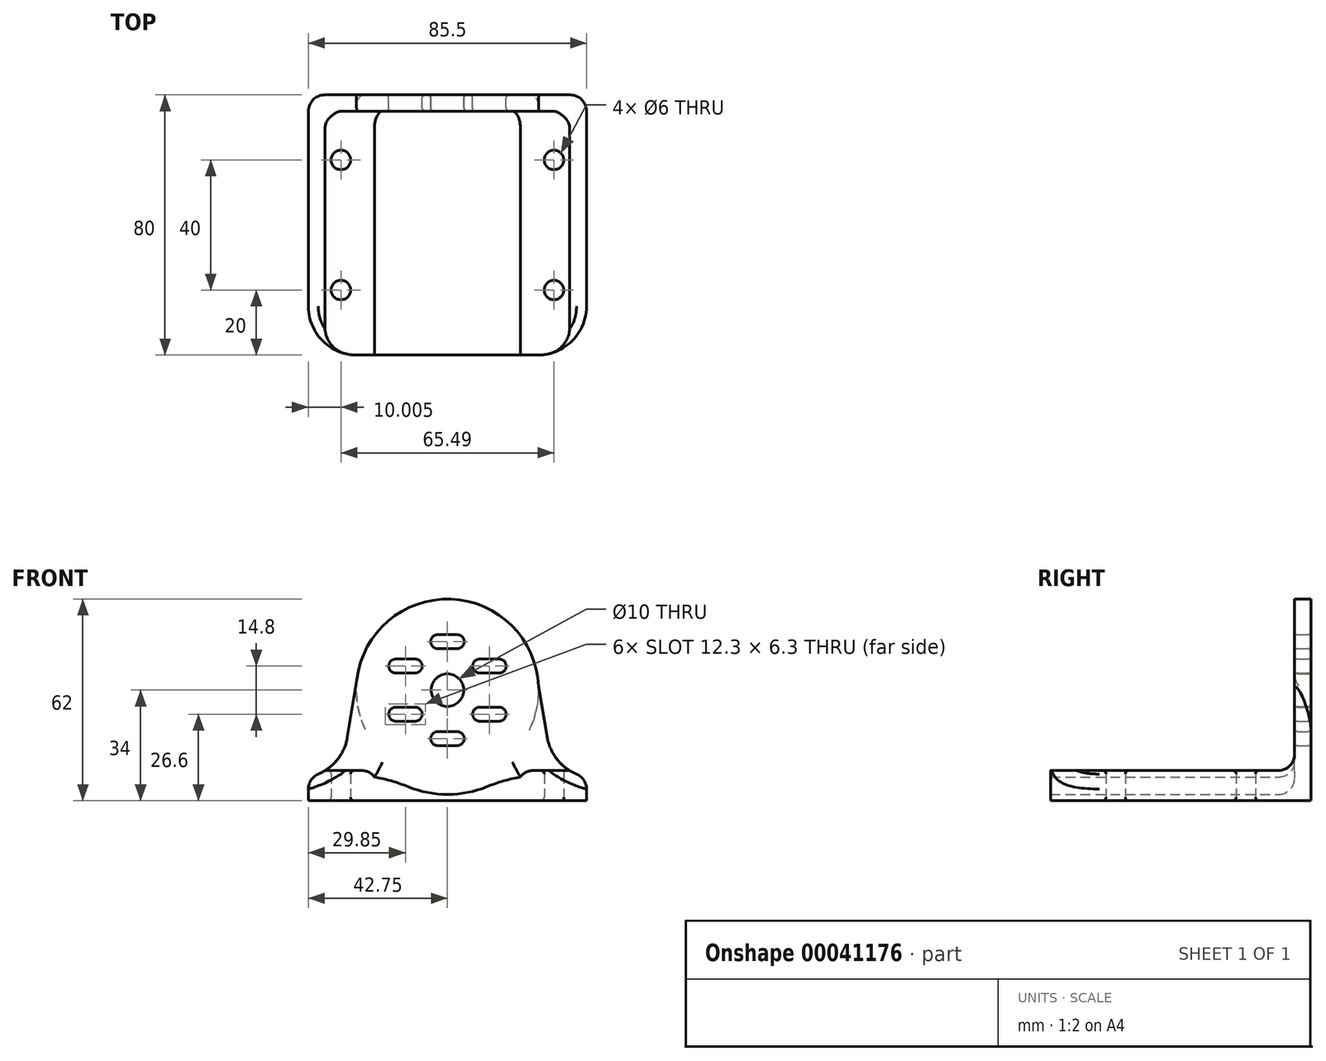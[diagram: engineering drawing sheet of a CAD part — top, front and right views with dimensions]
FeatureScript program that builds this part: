
annotation { "Feature Type Name" : "Feature", "Feature Type Description" : "" }
export const myFeature = defineFeature(function(context is Context, id is Id, definition is map)
    precondition{}
    {
        {
            var Q0;
            Q0=qCreatedBy(makeId("Front.planeOp"),FACE);
            var sketch = newSketch(context, id + "F0", { "sketchPlane" : qUnion([Q0])});
            skCircle(sketch, "E0", {"center": v(0, 34) * mm, "radius": 5 * mm});
            skArc(sketch, "E1", {"start": v(27.98, 35.12) * mm, "mid": v(1.08, 61.98) * mm, "end": v(-27.8, 37.27) * mm});
            skLineSegment(sketch, "E2", {"start": v(69.96, 34) * mm, "end": v(-14.46, 34) * mm, "construction": true});
            skLineSegment(sketch, "E3", {"start": v(64.8, 41.4) * mm, "end": v(-20.7, 41.4) * mm, "construction": true});
            skLineSegment(sketch, "E4", {"start": v(64.8, 26.6) * mm, "end": v(-20.7, 26.6) * mm, "construction": true});
            skLineSegment(sketch, "E5", {"start": v(0, 53.75) * mm, "end": v(0, -13.12) * mm, "construction": true});
            skLineSegment(sketch, "E6", {"start": v(12.9, 75.4) * mm, "end": v(12.9, 29.57) * mm, "construction": true});
            skLineSegment(sketch, "E7", {"start": v(-12.9, 75.4) * mm, "end": v(-12.9, 29.57) * mm, "construction": true});
            skArc(sketch, "E8", {"start": v(9.9, 28.75) * mm, "mid": v(7.75, 26.6) * mm, "end": v(9.9, 24.45) * mm});
            skArc(sketch, "E9", {"start": v(15.9, 24.45) * mm, "mid": v(18.05, 26.6) * mm, "end": v(15.9, 28.75) * mm});
            skLineSegment(sketch, "E10", {"start": v(15.9, 28.75) * mm, "end": v(9.9, 28.75) * mm});
            skLineSegment(sketch, "E11", {"start": v(15.9, 24.45) * mm, "end": v(9.9, 24.45) * mm});
            skLineSegment(sketch, "E12", {"start": v(15.9, 26.6) * mm, "end": v(12.9, 26.6) * mm});
            skLineSegment(sketch, "E13", {"start": v(12.9, 26.6) * mm, "end": v(9.9, 26.6) * mm});
            skArc(sketch, "E14", {"start": v(9.9, 43.55) * mm, "mid": v(7.75, 41.4) * mm, "end": v(9.9, 39.25) * mm});
            skArc(sketch, "E15", {"start": v(15.9, 39.25) * mm, "mid": v(18.05, 41.4) * mm, "end": v(15.9, 43.55) * mm});
            skLineSegment(sketch, "E16", {"start": v(15.9, 43.55) * mm, "end": v(9.9, 43.55) * mm});
            skLineSegment(sketch, "E17", {"start": v(15.9, 39.25) * mm, "end": v(9.9, 39.25) * mm});
            skLineSegment(sketch, "E18", {"start": v(15.9, 41.4) * mm, "end": v(12.9, 41.4) * mm});
            skLineSegment(sketch, "E19", {"start": v(12.9, 41.4) * mm, "end": v(9.9, 41.4) * mm});
            skArc(sketch, "E20", {"start": v(-15.9, 28.75) * mm, "mid": v(-18.05, 26.6) * mm, "end": v(-15.9, 24.45) * mm});
            skArc(sketch, "E21", {"start": v(-9.9, 24.45) * mm, "mid": v(-7.75, 26.6) * mm, "end": v(-9.9, 28.75) * mm});
            skLineSegment(sketch, "E22", {"start": v(-9.9, 28.75) * mm, "end": v(-15.9, 28.75) * mm});
            skLineSegment(sketch, "E23", {"start": v(-9.9, 24.45) * mm, "end": v(-15.9, 24.45) * mm});
            skLineSegment(sketch, "E24", {"start": v(-9.9, 26.6) * mm, "end": v(-12.9, 26.6) * mm});
            skLineSegment(sketch, "E25", {"start": v(-12.9, 26.6) * mm, "end": v(-15.9, 26.6) * mm});
            skArc(sketch, "E26", {"start": v(-3, 51.05) * mm, "mid": v(-5.15, 48.9) * mm, "end": v(-3, 46.75) * mm});
            skArc(sketch, "E27", {"start": v(3, 46.75) * mm, "mid": v(5.15, 48.9) * mm, "end": v(3, 51.05) * mm});
            skLineSegment(sketch, "E28", {"start": v(3, 51.05) * mm, "end": v(-3, 51.05) * mm});
            skLineSegment(sketch, "E29", {"start": v(3, 46.75) * mm, "end": v(-3, 46.75) * mm});
            skLineSegment(sketch, "E30", {"start": v(3, 48.9) * mm, "end": v(0, 48.9) * mm});
            skLineSegment(sketch, "E31", {"start": v(0, 48.9) * mm, "end": v(-3, 48.9) * mm});
            skArc(sketch, "E32", {"start": v(-3, 21.25) * mm, "mid": v(-5.15, 19.1) * mm, "end": v(-3, 16.95) * mm});
            skArc(sketch, "E33", {"start": v(3, 16.95) * mm, "mid": v(5.15, 19.1) * mm, "end": v(3, 21.25) * mm});
            skLineSegment(sketch, "E34", {"start": v(3, 21.25) * mm, "end": v(-3, 21.25) * mm});
            skLineSegment(sketch, "E35", {"start": v(3, 16.95) * mm, "end": v(-3, 16.95) * mm});
            skLineSegment(sketch, "E36", {"start": v(3, 19.1) * mm, "end": v(0, 19.1) * mm});
            skLineSegment(sketch, "E37", {"start": v(0, 19.1) * mm, "end": v(-3, 19.1) * mm});
            skArc(sketch, "E38", {"start": v(-15.9, 43.55) * mm, "mid": v(-18.05, 41.4) * mm, "end": v(-15.9, 39.25) * mm});
            skArc(sketch, "E39", {"start": v(-9.9, 39.25) * mm, "mid": v(-7.75, 41.4) * mm, "end": v(-9.9, 43.55) * mm});
            skLineSegment(sketch, "E40", {"start": v(-9.9, 43.55) * mm, "end": v(-15.9, 43.55) * mm});
            skLineSegment(sketch, "E41", {"start": v(-9.9, 39.25) * mm, "end": v(-15.9, 39.25) * mm});
            skLineSegment(sketch, "E42", {"start": v(-9.9, 41.4) * mm, "end": v(-12.9, 41.4) * mm});
            skLineSegment(sketch, "E43", {"start": v(-12.9, 41.4) * mm, "end": v(-15.9, 41.4) * mm});
            skLineSegment(sketch, "E44", {"start": v(58.97, 48.9) * mm, "end": v(-4.8, 48.9) * mm, "construction": true});
            skLineSegment(sketch, "E45", {"start": v(4.8, 19.1) * mm, "end": v(-4.8, 19.1) * mm, "construction": true});
            skLineSegment(sketch, "E46", {"start": v(0, 0) * mm, "end": v(-32.75, 0) * mm});
            skLineSegment(sketch, "E47", {"start": v(0, 0) * mm, "end": v(32.75, 0) * mm});
            skLineSegment(sketch, "E48", {"start": v(-46.8, 7.28) * mm, "end": v(29.3, 7.28) * mm, "construction": true});
            skLineSegment(sketch, "E49", {"start": v(-32.75, 7.28) * mm, "end": v(-27.8, 37.27) * mm});
            skLineSegment(sketch, "E50", {"start": v(29.3, 7.28) * mm, "end": v(47.8, 7.28) * mm, "construction": true});
            skLineSegment(sketch, "E51", {"start": v(32.75, 7.28) * mm, "end": v(27.98, 35.12) * mm});
            skLineSegment(sketch, "E52", {"start": v(-32.75, 7.28) * mm, "end": v(-32.75, 0) * mm});
            skLineSegment(sketch, "E53", {"start": v(32.75, 7.28) * mm, "end": v(32.75, 0) * mm});
            skLineSegment(sketch, "E54", {"start": v(-22.42, 7.28) * mm, "end": v(-17.76, 7.28) * mm});
            skArc(sketch, "E55", {"start": v(-17.76, 7.28) * mm, "mid": v(0, 1.91) * mm, "end": v(17.76, 7.28) * mm});
            skLineSegment(sketch, "E56.trimOffspring", {"start": v(17.76, 7.28) * mm, "end": v(22.42, 7.28) * mm});
            skLineSegment(sketch, "E57", {"start": v(-22.42, 7.28) * mm, "end": v(-22.42, 9.28) * mm});
            skLineSegment(sketch, "E58", {"start": v(-22.42, 9.28) * mm, "end": v(-32.42, 9.28) * mm});
            skLineSegment(sketch, "E59", {"start": v(22.42, 7.28) * mm, "end": v(22.42, 9.28) * mm});
            skLineSegment(sketch, "E60", {"start": v(22.42, 9.28) * mm, "end": v(32.4, 9.28) * mm});
            skLineSegment(sketch, "E61.trimOffspring", {"start": v(29.3, 7.28) * mm, "end": v(32.75, 7.28) * mm});
            skSolve(sketch);
        }
        {
            var Q0;
            Q0=makeQuery(id+"F0.imprint","IMPRINT",FACE,{"disambiguationData":[TD([[makeQuery(id+"F0.imprint","IMPRINT",EDGE,{"derivedFrom":sQuery(id+"F0.wireOp",EDGE,"E0")}),-1.0]])]});
            extrude(context, id + "F1", {"entities" : qUnion([Q0]), "depth" : 5 * mm});
        }
        {
            var Q0;
            Q0=makeQuery(id+"F0.imprint","IMPRINT",FACE,{"disambiguationData":[TD([[makeQuery(id+"F0.imprint","IMPRINT",EDGE,{"derivedFrom":sQuery(id+"F0.wireOp",EDGE,"E46")}),-1.0]])]});
            extrude(context, id + "F2", {"entities" : qUnion([Q0]), "operationType" : NewBodyOperationType.ADD, "depth" : 80 * mm});
        }
        {
            var Q0;
            Q0=makeQuery(id+"F2.opExtrude","SWEPT_EDGE",EDGE,{"disambiguationData":[OSD([sQuery(id+"F0.wireOp",EDGE,"E54"),sQuery(id+"F0.wireOp",EDGE,"E55")])]});
            var Q1;
            Q1=makeQuery(id+"F2.opExtrude","SWEPT_EDGE",EDGE,{"disambiguationData":[OSD([sQuery(id+"F0.wireOp",EDGE,"E55"),sQuery(id+"F0.wireOp",EDGE,"E56.trimOffspring")])]});
            fillet(context, id + "F3", {"entities" : qUnion([Q0, Q1]), "radius" : 50 * mm, "tangentPropagation" : true, "allowEdgeOverflow" : false});
        }
        {
            var Q0;
            Q0=makeQuery(id+"F1.opExtrude","CAP_EDGE",EDGE,{"disambiguationData":[OSD([sQuery(id+"F0.wireOp",EDGE,"E17")])],"isStart":true});
            var Q1;
            Q1=makeQuery(id+"F1.opExtrude","CAP_EDGE",EDGE,{"disambiguationData":[OSD([sQuery(id+"F0.wireOp",EDGE,"E11")])],"isStart":true});
            var Q2;
            Q2=makeQuery(id+"F1.opExtrude","CAP_EDGE",EDGE,{"disambiguationData":[OSD([sQuery(id+"F0.wireOp",EDGE,"E34")])],"isStart":true});
            var Q3;
            Q3=makeQuery(id+"F1.opExtrude","CAP_EDGE",EDGE,{"disambiguationData":[OSD([sQuery(id+"F0.wireOp",EDGE,"E0")])],"isStart":true});
            var Q4;
            Q4=makeQuery(id+"F1.opExtrude","CAP_EDGE",EDGE,{"disambiguationData":[OSD([sQuery(id+"F0.wireOp",EDGE,"E22")])],"isStart":true});
            var Q5;
            Q5=makeQuery(id+"F1.opExtrude","CAP_EDGE",EDGE,{"disambiguationData":[OSD([sQuery(id+"F0.wireOp",EDGE,"E41")])],"isStart":true});
            var Q6;
            Q6=makeQuery(id+"F1.opExtrude","CAP_EDGE",EDGE,{"disambiguationData":[OSD([sQuery(id+"F0.wireOp",EDGE,"E29")])],"isStart":true});
            var Q7;
            Q7=makeQuery(id+"F1.opExtrude","CAP_EDGE",EDGE,{"disambiguationData":[OSD([sQuery(id+"F0.wireOp",EDGE,"E17")])],"isStart":false});
            var Q8;
            Q8=makeQuery(id+"F1.opExtrude","CAP_EDGE",EDGE,{"disambiguationData":[OSD([sQuery(id+"F0.wireOp",EDGE,"E11")])],"isStart":false});
            var Q9;
            Q9=makeQuery(id+"F1.opExtrude","CAP_EDGE",EDGE,{"disambiguationData":[OSD([sQuery(id+"F0.wireOp",EDGE,"E35")])],"isStart":false});
            var Q10;
            Q10=makeQuery(id+"F1.opExtrude","CAP_EDGE",EDGE,{"disambiguationData":[OSD([sQuery(id+"F0.wireOp",EDGE,"E0")])],"isStart":false});
            var Q11;
            Q11=makeQuery(id+"F1.opExtrude","CAP_EDGE",EDGE,{"disambiguationData":[OSD([sQuery(id+"F0.wireOp",EDGE,"E23")])],"isStart":false});
            var Q12;
            Q12=makeQuery(id+"F1.opExtrude","CAP_EDGE",EDGE,{"disambiguationData":[OSD([sQuery(id+"F0.wireOp",EDGE,"E41")])],"isStart":false});
            var Q13;
            Q13=makeQuery(id+"F1.opExtrude","CAP_EDGE",EDGE,{"disambiguationData":[OSD([sQuery(id+"F0.wireOp",EDGE,"E29")])],"isStart":false});
            fillet(context, id + "F4", {"entities" : qUnion([Q0, Q1, Q2, Q3, Q4, Q5, Q6, Q7, Q8, Q9, Q10, Q11, Q12, Q13]), "radius" : 1 * mm, "tangentPropagation" : true, "allowEdgeOverflow" : false});
        }
        {
            var Q0;
            Q0=makeQuery(id+"F2.opExtrude","SWEPT_FACE",FACE,{"disambiguationData":[OSD([sQuery(id+"F0.wireOp",EDGE,"E53")])]});
            extrude(context, id + "F5", {"entities" : qUnion([Q0]), "operationType" : NewBodyOperationType.ADD, "depth" : 10 * mm});
        }
        {
            var Q0;
            Q0=makeQuery(id+"F2.opExtrude","SWEPT_FACE",FACE,{"disambiguationData":[OSD([sQuery(id+"F0.wireOp",EDGE,"E52")])]});
            extrude(context, id + "F6", {"entities" : qUnion([Q0]), "operationType" : NewBodyOperationType.ADD, "depth" : 10 * mm});
        }
        {
            var Q0;
            {var subQ0=sQuery(id+"F0.wireOp",EDGE,"E52");Q0=makeQuery(id+"F6.opExtrude","CAP_EDGE",EDGE,{"disambiguationData":[OSD([subQ0]),TDD([makeQuery(id+"F2.opExtrude","CAP_EDGE",EDGE,{"disambiguationData":[OSD([subQ0])],"isStart":false})])],"isStart":false});}
            var Q1;
            {var subQ0=sQuery(id+"F0.wireOp",EDGE,"E53");Q1=makeQuery(id+"F5.opExtrude","CAP_EDGE",EDGE,{"disambiguationData":[OSD([subQ0]),TDD([makeQuery(id+"F2.opExtrude","CAP_EDGE",EDGE,{"disambiguationData":[OSD([subQ0])],"isStart":false})])],"isStart":false});}
            fillet(context, id + "F7", {"entities" : qUnion([Q0, Q1]), "radius" : 15 * mm, "tangentPropagation" : true, "allowEdgeOverflow" : false});
        }
        {
            var Q0;
            {var subQ0=sQuery(id+"F0.wireOp",EDGE,"E49");var subQ1=sQuery(id+"F0.wireOp",EDGE,"E52");var subQ2=sQuery(id+"F0.wireOp",EDGE,"E54");Q0=makeQuery(id+"F6.boolean.opBoolean","MERGE",EDGE,{"derivedFrom":[makeQuery(id+"F2.boolean.opBoolean","MERGE",EDGE,{"derivedFrom":[makeQuery(id+"F1.opExtrude","SWEPT_EDGE",EDGE,{"disambiguationData":[OSD([subQ0,subQ1,subQ2])]}),makeQuery(id+"F2.opExtrude","SWEPT_EDGE",EDGE,{"disambiguationData":[OSD([subQ0,subQ1,subQ2])]})]}),makeQuery(id+"F6.opExtrude","CAP_EDGE",EDGE,{"disambiguationData":[OSD([subQ0,subQ1,subQ2])],"isStart":true})]});}
            var Q1;
            {var subQ0=sQuery(id+"F0.wireOp",EDGE,"E51");var subQ1=sQuery(id+"F0.wireOp",EDGE,"E53");var subQ2=sQuery(id+"F0.wireOp",EDGE,"E56.trimOffspring");Q1=makeQuery(id+"F5.boolean.opBoolean","MERGE",EDGE,{"derivedFrom":[makeQuery(id+"F2.boolean.opBoolean","MERGE",EDGE,{"derivedFrom":[makeQuery(id+"F1.opExtrude","SWEPT_EDGE",EDGE,{"disambiguationData":[OSD([subQ0,subQ1,subQ2])]}),makeQuery(id+"F2.opExtrude","SWEPT_EDGE",EDGE,{"disambiguationData":[OSD([subQ0,subQ1,subQ2])]})]}),makeQuery(id+"F5.opExtrude","CAP_EDGE",EDGE,{"disambiguationData":[OSD([subQ0,subQ1,subQ2])],"isStart":true})]});}
            fillet(context, id + "F8", {"entities" : qUnion([Q0, Q1]), "radius" : 15 * mm, "tangentPropagation" : true, "allowEdgeOverflow" : false});
        }
        {
            var Q0;
            {var subQ0=sQuery(id+"F0.wireOp",EDGE,"E53");Q0=makeQuery(id+"F5.opExtrude","CAP_EDGE",EDGE,{"disambiguationData":[OSD([subQ0]),TDD([makeQuery(id+"F2.opExtrude","CAP_EDGE",EDGE,{"disambiguationData":[OSD([subQ0])],"isStart":true})])],"isStart":false});}
            var Q1;
            {var subQ0=sQuery(id+"F0.wireOp",EDGE,"E52");Q1=makeQuery(id+"F6.opExtrude","CAP_EDGE",EDGE,{"disambiguationData":[OSD([subQ0]),TDD([makeQuery(id+"F2.opExtrude","CAP_EDGE",EDGE,{"disambiguationData":[OSD([subQ0])],"isStart":true})])],"isStart":false});}
            var Q2;
            {var subQ0=sQuery(id+"F0.wireOp",EDGE,"E51");var subQ1=sQuery(id+"F0.wireOp",EDGE,"E53");var subQ2=sQuery(id+"F0.wireOp",EDGE,"E56.trimOffspring");Q2=makeQuery(id+"F8.opFillet","BLEND_EDGE",EDGE,{"blendedFrom":[makeQuery(id+"F5.boolean.opBoolean","MERGE",EDGE,{"derivedFrom":[makeQuery(id+"F2.boolean.opBoolean","MERGE",EDGE,{"derivedFrom":[makeQuery(id+"F1.opExtrude","SWEPT_EDGE",EDGE,{"disambiguationData":[OSD([subQ0,subQ1,subQ2])]}),makeQuery(id+"F2.opExtrude","SWEPT_EDGE",EDGE,{"disambiguationData":[OSD([subQ0,subQ1,subQ2])]})]}),makeQuery(id+"F5.opExtrude","CAP_EDGE",EDGE,{"disambiguationData":[OSD([subQ0,subQ1,subQ2])],"isStart":true})]}),makeQuery(id+"F5.opExtrude","CAP_FACE",FACE,{"disambiguationData":[OSD([subQ1])],"isStart":false})],"blendedInto":[makeQuery(id+"F5.opExtrude","CAP_FACE",FACE,{"disambiguationData":[OSD([subQ1])],"isStart":false})]});}
            var Q3;
            {var subQ0=sQuery(id+"F0.wireOp",EDGE,"E51");var subQ1=sQuery(id+"F0.wireOp",EDGE,"E53");var subQ2=sQuery(id+"F0.wireOp",EDGE,"E56.trimOffspring");var subQ3=sQuery(id+"F0.wireOp",EDGE,"E54");var subQ4=sQuery(id+"F0.wireOp",EDGE,"E55");var subQ5=sQuery(id+"F0.wireOp",EDGE,"E52");Q3=makeQuery(id+"F8.opFillet","BLEND_EDGE",EDGE,{"blendedFrom":[makeQuery(id+"F5.boolean.opBoolean","MERGE",EDGE,{"derivedFrom":[makeQuery(id+"F2.boolean.opBoolean","MERGE",EDGE,{"derivedFrom":[makeQuery(id+"F1.opExtrude","SWEPT_EDGE",EDGE,{"disambiguationData":[OSD([subQ0,subQ1,subQ2])]}),makeQuery(id+"F2.opExtrude","SWEPT_EDGE",EDGE,{"disambiguationData":[OSD([subQ0,subQ1,subQ2])]})]}),makeQuery(id+"F5.opExtrude","CAP_EDGE",EDGE,{"disambiguationData":[OSD([subQ0,subQ1,subQ2])],"isStart":true})]}),makeQuery(id+"F6.boolean.opBoolean","MERGE",FACE,{"derivedFrom":[makeQuery(id+"F5.boolean.opBoolean","MERGE",FACE,{"derivedFrom":[makeQuery(id+"F2.boolean.opBoolean","MERGE",FACE,{"derivedFrom":[makeQuery(id+"F1.opExtrude","CAP_FACE",FACE,{"disambiguationData":[OSD([sQuery(id+"F0.wireOp",EDGE,"E0"),sQuery(id+"F0.wireOp",EDGE,"E1"),sQuery(id+"F0.wireOp",EDGE,"E8"),sQuery(id+"F0.wireOp",EDGE,"E9"),sQuery(id+"F0.wireOp",EDGE,"E10"),sQuery(id+"F0.wireOp",EDGE,"E11"),sQuery(id+"F0.wireOp",EDGE,"E14"),sQuery(id+"F0.wireOp",EDGE,"E15"),sQuery(id+"F0.wireOp",EDGE,"E16"),sQuery(id+"F0.wireOp",EDGE,"E17"),sQuery(id+"F0.wireOp",EDGE,"E20"),sQuery(id+"F0.wireOp",EDGE,"E21"),sQuery(id+"F0.wireOp",EDGE,"E22"),sQuery(id+"F0.wireOp",EDGE,"E23"),sQuery(id+"F0.wireOp",EDGE,"E26"),sQuery(id+"F0.wireOp",EDGE,"E27"),sQuery(id+"F0.wireOp",EDGE,"E28"),sQuery(id+"F0.wireOp",EDGE,"E29"),sQuery(id+"F0.wireOp",EDGE,"E32"),sQuery(id+"F0.wireOp",EDGE,"E33"),sQuery(id+"F0.wireOp",EDGE,"E34"),sQuery(id+"F0.wireOp",EDGE,"E35"),sQuery(id+"F0.wireOp",EDGE,"E38"),sQuery(id+"F0.wireOp",EDGE,"E39"),sQuery(id+"F0.wireOp",EDGE,"E40"),sQuery(id+"F0.wireOp",EDGE,"E41"),sQuery(id+"F0.wireOp",EDGE,"E49"),subQ0,subQ3,subQ4,subQ2])],"isStart":true}),makeQuery(id+"F2.opExtrude","CAP_FACE",FACE,{"disambiguationData":[OSD([sQuery(id+"F0.wireOp",EDGE,"E46"),sQuery(id+"F0.wireOp",EDGE,"E47"),subQ5,subQ1,subQ3,subQ4,subQ2])],"isStart":true})]}),makeQuery(id+"F5.opExtrude","SWEPT_FACE",FACE,{"disambiguationData":[OSD([subQ1]),TDD([makeQuery(id+"F2.opExtrude","CAP_EDGE",EDGE,{"disambiguationData":[OSD([subQ1])],"isStart":true})])]})]}),makeQuery(id+"F6.opExtrude","SWEPT_FACE",FACE,{"disambiguationData":[OSD([subQ5]),TDD([makeQuery(id+"F2.opExtrude","CAP_EDGE",EDGE,{"disambiguationData":[OSD([subQ5])],"isStart":true})])]})]})],"blendedInto":[makeQuery(id+"F6.boolean.opBoolean","MERGE",FACE,{"derivedFrom":[makeQuery(id+"F5.boolean.opBoolean","MERGE",FACE,{"derivedFrom":[makeQuery(id+"F2.boolean.opBoolean","MERGE",FACE,{"derivedFrom":[makeQuery(id+"F1.opExtrude","CAP_FACE",FACE,{"disambiguationData":[OSD([sQuery(id+"F0.wireOp",EDGE,"E0"),sQuery(id+"F0.wireOp",EDGE,"E1"),sQuery(id+"F0.wireOp",EDGE,"E8"),sQuery(id+"F0.wireOp",EDGE,"E9"),sQuery(id+"F0.wireOp",EDGE,"E10"),sQuery(id+"F0.wireOp",EDGE,"E11"),sQuery(id+"F0.wireOp",EDGE,"E14"),sQuery(id+"F0.wireOp",EDGE,"E15"),sQuery(id+"F0.wireOp",EDGE,"E16"),sQuery(id+"F0.wireOp",EDGE,"E17"),sQuery(id+"F0.wireOp",EDGE,"E20"),sQuery(id+"F0.wireOp",EDGE,"E21"),sQuery(id+"F0.wireOp",EDGE,"E22"),sQuery(id+"F0.wireOp",EDGE,"E23"),sQuery(id+"F0.wireOp",EDGE,"E26"),sQuery(id+"F0.wireOp",EDGE,"E27"),sQuery(id+"F0.wireOp",EDGE,"E28"),sQuery(id+"F0.wireOp",EDGE,"E29"),sQuery(id+"F0.wireOp",EDGE,"E32"),sQuery(id+"F0.wireOp",EDGE,"E33"),sQuery(id+"F0.wireOp",EDGE,"E34"),sQuery(id+"F0.wireOp",EDGE,"E35"),sQuery(id+"F0.wireOp",EDGE,"E38"),sQuery(id+"F0.wireOp",EDGE,"E39"),sQuery(id+"F0.wireOp",EDGE,"E40"),sQuery(id+"F0.wireOp",EDGE,"E41"),sQuery(id+"F0.wireOp",EDGE,"E49"),subQ0,subQ3,subQ4,subQ2])],"isStart":true}),makeQuery(id+"F2.opExtrude","CAP_FACE",FACE,{"disambiguationData":[OSD([sQuery(id+"F0.wireOp",EDGE,"E46"),sQuery(id+"F0.wireOp",EDGE,"E47"),subQ5,subQ1,subQ3,subQ4,subQ2])],"isStart":true})]}),makeQuery(id+"F5.opExtrude","SWEPT_FACE",FACE,{"disambiguationData":[OSD([subQ1]),TDD([makeQuery(id+"F2.opExtrude","CAP_EDGE",EDGE,{"disambiguationData":[OSD([subQ1])],"isStart":true})])]})]}),makeQuery(id+"F6.opExtrude","SWEPT_FACE",FACE,{"disambiguationData":[OSD([subQ5]),TDD([makeQuery(id+"F2.opExtrude","CAP_EDGE",EDGE,{"disambiguationData":[OSD([subQ5])],"isStart":true})])]})]})]});}
            var Q4;
            {var subQ0=sQuery(id+"F0.wireOp",EDGE,"E49");var subQ1=sQuery(id+"F0.wireOp",EDGE,"E52");var subQ2=sQuery(id+"F0.wireOp",EDGE,"E54");Q4=makeQuery(id+"F8.opFillet","BLEND_EDGE",EDGE,{"blendedFrom":[makeQuery(id+"F6.boolean.opBoolean","MERGE",EDGE,{"derivedFrom":[makeQuery(id+"F2.boolean.opBoolean","MERGE",EDGE,{"derivedFrom":[makeQuery(id+"F1.opExtrude","SWEPT_EDGE",EDGE,{"disambiguationData":[OSD([subQ0,subQ1,subQ2])]}),makeQuery(id+"F2.opExtrude","SWEPT_EDGE",EDGE,{"disambiguationData":[OSD([subQ0,subQ1,subQ2])]})]}),makeQuery(id+"F6.opExtrude","CAP_EDGE",EDGE,{"disambiguationData":[OSD([subQ0,subQ1,subQ2])],"isStart":true})]}),makeQuery(id+"F6.opExtrude","CAP_FACE",FACE,{"disambiguationData":[OSD([subQ1])],"isStart":false})],"blendedInto":[makeQuery(id+"F6.opExtrude","CAP_FACE",FACE,{"disambiguationData":[OSD([subQ1])],"isStart":false})]});}
            var Q5;
            {var subQ0=sQuery(id+"F0.wireOp",EDGE,"E49");var subQ1=sQuery(id+"F0.wireOp",EDGE,"E52");var subQ2=sQuery(id+"F0.wireOp",EDGE,"E54");var subQ3=sQuery(id+"F0.wireOp",EDGE,"E55");var subQ4=sQuery(id+"F0.wireOp",EDGE,"E56.trimOffspring");var subQ5=sQuery(id+"F0.wireOp",EDGE,"E53");Q5=makeQuery(id+"F8.opFillet","BLEND_EDGE",EDGE,{"blendedFrom":[makeQuery(id+"F6.boolean.opBoolean","MERGE",EDGE,{"derivedFrom":[makeQuery(id+"F2.boolean.opBoolean","MERGE",EDGE,{"derivedFrom":[makeQuery(id+"F1.opExtrude","SWEPT_EDGE",EDGE,{"disambiguationData":[OSD([subQ0,subQ1,subQ2])]}),makeQuery(id+"F2.opExtrude","SWEPT_EDGE",EDGE,{"disambiguationData":[OSD([subQ0,subQ1,subQ2])]})]}),makeQuery(id+"F6.opExtrude","CAP_EDGE",EDGE,{"disambiguationData":[OSD([subQ0,subQ1,subQ2])],"isStart":true})]}),makeQuery(id+"F6.boolean.opBoolean","MERGE",FACE,{"derivedFrom":[makeQuery(id+"F5.boolean.opBoolean","MERGE",FACE,{"derivedFrom":[makeQuery(id+"F2.boolean.opBoolean","MERGE",FACE,{"derivedFrom":[makeQuery(id+"F1.opExtrude","CAP_FACE",FACE,{"disambiguationData":[OSD([sQuery(id+"F0.wireOp",EDGE,"E0"),sQuery(id+"F0.wireOp",EDGE,"E1"),sQuery(id+"F0.wireOp",EDGE,"E8"),sQuery(id+"F0.wireOp",EDGE,"E9"),sQuery(id+"F0.wireOp",EDGE,"E10"),sQuery(id+"F0.wireOp",EDGE,"E11"),sQuery(id+"F0.wireOp",EDGE,"E14"),sQuery(id+"F0.wireOp",EDGE,"E15"),sQuery(id+"F0.wireOp",EDGE,"E16"),sQuery(id+"F0.wireOp",EDGE,"E17"),sQuery(id+"F0.wireOp",EDGE,"E20"),sQuery(id+"F0.wireOp",EDGE,"E21"),sQuery(id+"F0.wireOp",EDGE,"E22"),sQuery(id+"F0.wireOp",EDGE,"E23"),sQuery(id+"F0.wireOp",EDGE,"E26"),sQuery(id+"F0.wireOp",EDGE,"E27"),sQuery(id+"F0.wireOp",EDGE,"E28"),sQuery(id+"F0.wireOp",EDGE,"E29"),sQuery(id+"F0.wireOp",EDGE,"E32"),sQuery(id+"F0.wireOp",EDGE,"E33"),sQuery(id+"F0.wireOp",EDGE,"E34"),sQuery(id+"F0.wireOp",EDGE,"E35"),sQuery(id+"F0.wireOp",EDGE,"E38"),sQuery(id+"F0.wireOp",EDGE,"E39"),sQuery(id+"F0.wireOp",EDGE,"E40"),sQuery(id+"F0.wireOp",EDGE,"E41"),subQ0,sQuery(id+"F0.wireOp",EDGE,"E51"),subQ2,subQ3,subQ4])],"isStart":true}),makeQuery(id+"F2.opExtrude","CAP_FACE",FACE,{"disambiguationData":[OSD([sQuery(id+"F0.wireOp",EDGE,"E46"),sQuery(id+"F0.wireOp",EDGE,"E47"),subQ1,subQ5,subQ2,subQ3,subQ4])],"isStart":true})]}),makeQuery(id+"F5.opExtrude","SWEPT_FACE",FACE,{"disambiguationData":[OSD([subQ5]),TDD([makeQuery(id+"F2.opExtrude","CAP_EDGE",EDGE,{"disambiguationData":[OSD([subQ5])],"isStart":true})])]})]}),makeQuery(id+"F6.opExtrude","SWEPT_FACE",FACE,{"disambiguationData":[OSD([subQ1]),TDD([makeQuery(id+"F2.opExtrude","CAP_EDGE",EDGE,{"disambiguationData":[OSD([subQ1])],"isStart":true})])]})]})],"blendedInto":[makeQuery(id+"F6.boolean.opBoolean","MERGE",FACE,{"derivedFrom":[makeQuery(id+"F5.boolean.opBoolean","MERGE",FACE,{"derivedFrom":[makeQuery(id+"F2.boolean.opBoolean","MERGE",FACE,{"derivedFrom":[makeQuery(id+"F1.opExtrude","CAP_FACE",FACE,{"disambiguationData":[OSD([sQuery(id+"F0.wireOp",EDGE,"E0"),sQuery(id+"F0.wireOp",EDGE,"E1"),sQuery(id+"F0.wireOp",EDGE,"E8"),sQuery(id+"F0.wireOp",EDGE,"E9"),sQuery(id+"F0.wireOp",EDGE,"E10"),sQuery(id+"F0.wireOp",EDGE,"E11"),sQuery(id+"F0.wireOp",EDGE,"E14"),sQuery(id+"F0.wireOp",EDGE,"E15"),sQuery(id+"F0.wireOp",EDGE,"E16"),sQuery(id+"F0.wireOp",EDGE,"E17"),sQuery(id+"F0.wireOp",EDGE,"E20"),sQuery(id+"F0.wireOp",EDGE,"E21"),sQuery(id+"F0.wireOp",EDGE,"E22"),sQuery(id+"F0.wireOp",EDGE,"E23"),sQuery(id+"F0.wireOp",EDGE,"E26"),sQuery(id+"F0.wireOp",EDGE,"E27"),sQuery(id+"F0.wireOp",EDGE,"E28"),sQuery(id+"F0.wireOp",EDGE,"E29"),sQuery(id+"F0.wireOp",EDGE,"E32"),sQuery(id+"F0.wireOp",EDGE,"E33"),sQuery(id+"F0.wireOp",EDGE,"E34"),sQuery(id+"F0.wireOp",EDGE,"E35"),sQuery(id+"F0.wireOp",EDGE,"E38"),sQuery(id+"F0.wireOp",EDGE,"E39"),sQuery(id+"F0.wireOp",EDGE,"E40"),sQuery(id+"F0.wireOp",EDGE,"E41"),subQ0,sQuery(id+"F0.wireOp",EDGE,"E51"),subQ2,subQ3,subQ4])],"isStart":true}),makeQuery(id+"F2.opExtrude","CAP_FACE",FACE,{"disambiguationData":[OSD([sQuery(id+"F0.wireOp",EDGE,"E46"),sQuery(id+"F0.wireOp",EDGE,"E47"),subQ1,subQ5,subQ2,subQ3,subQ4])],"isStart":true})]}),makeQuery(id+"F5.opExtrude","SWEPT_FACE",FACE,{"disambiguationData":[OSD([subQ5]),TDD([makeQuery(id+"F2.opExtrude","CAP_EDGE",EDGE,{"disambiguationData":[OSD([subQ5])],"isStart":true})])]})]}),makeQuery(id+"F6.opExtrude","SWEPT_FACE",FACE,{"disambiguationData":[OSD([subQ1]),TDD([makeQuery(id+"F2.opExtrude","CAP_EDGE",EDGE,{"disambiguationData":[OSD([subQ1])],"isStart":true})])]})]})]});}
            fillet(context, id + "F9", {"entities" : qUnion([Q0, Q1, Q2, Q3, Q4, Q5]), "radius" : 5 * mm, "tangentPropagation" : true, "allowEdgeOverflow" : false});
        }
        {
            var Q0;
            Q0=makeQuery(id+"F2.opExtrude","SWEPT_EDGE",EDGE,{"disambiguationData":[OSD([sQuery(id+"F0.wireOp",EDGE,"E57"),sQuery(id+"F0.wireOp",EDGE,"E58")])]});
            var Q1;
            Q1=makeQuery(id+"F2.opExtrude","SWEPT_EDGE",EDGE,{"disambiguationData":[OSD([sQuery(id+"F0.wireOp",EDGE,"E59"),sQuery(id+"F0.wireOp",EDGE,"E60")])]});
            fillet(context, id + "F10", {"entities" : qUnion([Q0, Q1]), "radius" : 5 * mm, "allowEdgeOverflow" : false});
        }
        {
            var Q0;
            {var subQ0=sQuery(id+"F0.wireOp",EDGE,"E46");var subQ1=sQuery(id+"F0.wireOp",EDGE,"E47");Q0=makeQuery(id+"F6.boolean.opBoolean","MERGE",FACE,{"derivedFrom":[makeQuery(id+"F5.boolean.opBoolean","MERGE",FACE,{"derivedFrom":[makeQuery(id+"F2.opExtrude","SWEPT_FACE",FACE,{"disambiguationData":[OSD([subQ0,subQ1])]}),makeQuery(id+"F5.opExtrude","SWEPT_FACE",FACE,{"disambiguationData":[OSD([subQ1,sQuery(id+"F0.wireOp",EDGE,"E53")])]})]}),makeQuery(id+"F6.opExtrude","SWEPT_FACE",FACE,{"disambiguationData":[OSD([subQ0,sQuery(id+"F0.wireOp",EDGE,"E52")])]})]});}
            var sketch = newSketch(context, id + "F11", { "sketchPlane" : qUnion([Q0])});
            skLineSegment(sketch, "E62.0", {"start": v(37.75, 0) * mm, "end": v(-37.75, 0) * mm, "construction": true});
            skLineSegment(sketch, "E63.0", {"start": v(-42.75, 65) * mm, "end": v(-42.75, 5) * mm, "construction": true});
            skLineSegment(sketch, "E64.0", {"start": v(42.75, 65) * mm, "end": v(42.75, 5) * mm, "construction": true});
            skLineSegment(sketch, "E65.0", {"start": v(27.75, 80) * mm, "end": v(-27.75, 80) * mm, "construction": true});
            skLineSegment(sketch, "E66", {"start": v(0, 80) * mm, "end": v(0, 0) * mm, "construction": true});
            skCircle(sketch, "E67", {"center": v(-32.75, 60) * mm, "radius": 3 * mm});
            skLineSegment(sketch, "E68.0", {"start": v(5, 20) * mm, "end": v(-70.5, 20) * mm, "construction": true});
            skLineSegment(sketch, "E69.0", {"start": v(10.53, 82.3) * mm, "end": v(10.53, 22.3) * mm, "construction": true});
            skCircle(sketch, "E70", {"center": v(-32.75, 20) * mm, "radius": 3 * mm});
            skCircle(sketch, "E71", {"center": v(32.75, 60) * mm, "radius": 3 * mm});
            skCircle(sketch, "E72", {"center": v(32.75, 20) * mm, "radius": 3 * mm});
            skSolve(sketch);
        }
        {
            var Q0;
            Q0=makeQuery(id+"F11.imprint","IMPRINT",FACE,{"disambiguationData":[TD([[makeQuery(id+"F11.imprint","IMPRINT",EDGE,{"derivedFrom":sQuery(id+"F11.wireOp",EDGE,"E67")}),1.0]])]});
            var Q1;
            Q1=makeQuery(id+"F11.imprint","IMPRINT",FACE,{"disambiguationData":[TD([[makeQuery(id+"F11.imprint","IMPRINT",EDGE,{"derivedFrom":sQuery(id+"F11.wireOp",EDGE,"E70")}),1.0]])]});
            var Q2;
            Q2=makeQuery(id+"F11.imprint","IMPRINT",FACE,{"disambiguationData":[TD([[makeQuery(id+"F11.imprint","IMPRINT",EDGE,{"derivedFrom":sQuery(id+"F11.wireOp",EDGE,"E72")}),1.0]])]});
            var Q3;
            Q3=makeQuery(id+"F11.imprint","IMPRINT",FACE,{"disambiguationData":[TD([[makeQuery(id+"F11.imprint","IMPRINT",EDGE,{"derivedFrom":sQuery(id+"F11.wireOp",EDGE,"E71")}),1.0]])]});
            extrude(context, id + "F12", {"entities" : qUnion([Q0, Q1, Q2, Q3]), "operationType" : NewBodyOperationType.REMOVE, "endBound" : BoundingType.THROUGH_ALL, "oppositeDirection" : true, "depth" : 25 * mm});
        }
        {
            var Q0;
            Q0=makeQuery(id+"F12.boolean.opBoolean","COPY",FACE,{"derivedFrom":makeQuery(id+"F12.opExtrude","SWEPT_FACE",FACE,{"disambiguationData":[OSD([sQuery(id+"F11.wireOp",EDGE,"E71")])]})});
            var Q1;
            Q1=makeQuery(id+"F12.boolean.opBoolean","COPY",FACE,{"derivedFrom":makeQuery(id+"F12.opExtrude","SWEPT_FACE",FACE,{"disambiguationData":[OSD([sQuery(id+"F11.wireOp",EDGE,"E72")])]})});
            var Q2;
            Q2=makeQuery(id+"F12.boolean.opBoolean","COPY",FACE,{"derivedFrom":makeQuery(id+"F12.opExtrude","SWEPT_FACE",FACE,{"disambiguationData":[OSD([sQuery(id+"F11.wireOp",EDGE,"E70")])]})});
            var Q3;
            Q3=makeQuery(id+"F12.boolean.opBoolean","COPY",FACE,{"derivedFrom":makeQuery(id+"F12.opExtrude","SWEPT_FACE",FACE,{"disambiguationData":[OSD([sQuery(id+"F11.wireOp",EDGE,"E67")])]})});
            fillet(context, id + "F13", {"entities" : qUnion([Q0, Q1, Q2, Q3]), "radius" : 1 * mm, "tangentPropagation" : true, "allowEdgeOverflow" : false});
        }
        {
            var Q0;
            Q0=makeQuery(id+"F1.opExtrude","CAP_EDGE",EDGE,{"disambiguationData":[OSD([sQuery(id+"F0.wireOp",EDGE,"E55")])],"isStart":false});
            var Q1;
            {var subQ0=sQuery(id+"F0.wireOp",EDGE,"E54");var subQ1=sQuery(id+"F0.wireOp",EDGE,"E55");Q1=makeQuery(id+"F3.opFillet","BLEND_EDGE",EDGE,{"blendedFrom":[makeQuery(id+"F2.opExtrude","SWEPT_EDGE",EDGE,{"disambiguationData":[OSD([subQ0,subQ1])]}),makeQuery(id+"F1.opExtrude","CAP_FACE",FACE,{"disambiguationData":[OSD([sQuery(id+"F0.wireOp",EDGE,"E0"),sQuery(id+"F0.wireOp",EDGE,"E1"),sQuery(id+"F0.wireOp",EDGE,"E8"),sQuery(id+"F0.wireOp",EDGE,"E9"),sQuery(id+"F0.wireOp",EDGE,"E10"),sQuery(id+"F0.wireOp",EDGE,"E11"),sQuery(id+"F0.wireOp",EDGE,"E14"),sQuery(id+"F0.wireOp",EDGE,"E15"),sQuery(id+"F0.wireOp",EDGE,"E16"),sQuery(id+"F0.wireOp",EDGE,"E17"),sQuery(id+"F0.wireOp",EDGE,"E20"),sQuery(id+"F0.wireOp",EDGE,"E21"),sQuery(id+"F0.wireOp",EDGE,"E22"),sQuery(id+"F0.wireOp",EDGE,"E23"),sQuery(id+"F0.wireOp",EDGE,"E26"),sQuery(id+"F0.wireOp",EDGE,"E27"),sQuery(id+"F0.wireOp",EDGE,"E28"),sQuery(id+"F0.wireOp",EDGE,"E29"),sQuery(id+"F0.wireOp",EDGE,"E32"),sQuery(id+"F0.wireOp",EDGE,"E33"),sQuery(id+"F0.wireOp",EDGE,"E34"),sQuery(id+"F0.wireOp",EDGE,"E35"),sQuery(id+"F0.wireOp",EDGE,"E38"),sQuery(id+"F0.wireOp",EDGE,"E39"),sQuery(id+"F0.wireOp",EDGE,"E40"),sQuery(id+"F0.wireOp",EDGE,"E41"),sQuery(id+"F0.wireOp",EDGE,"E49"),sQuery(id+"F0.wireOp",EDGE,"E51"),subQ0,subQ1,sQuery(id+"F0.wireOp",EDGE,"E56.trimOffspring"),sQuery(id+"F0.wireOp",EDGE,"E57"),sQuery(id+"F0.wireOp",EDGE,"E58"),sQuery(id+"F0.wireOp",EDGE,"E59"),sQuery(id+"F0.wireOp",EDGE,"E60")])],"isStart":false})],"blendedInto":[makeQuery(id+"F1.opExtrude","CAP_FACE",FACE,{"disambiguationData":[OSD([sQuery(id+"F0.wireOp",EDGE,"E0"),sQuery(id+"F0.wireOp",EDGE,"E1"),sQuery(id+"F0.wireOp",EDGE,"E8"),sQuery(id+"F0.wireOp",EDGE,"E9"),sQuery(id+"F0.wireOp",EDGE,"E10"),sQuery(id+"F0.wireOp",EDGE,"E11"),sQuery(id+"F0.wireOp",EDGE,"E14"),sQuery(id+"F0.wireOp",EDGE,"E15"),sQuery(id+"F0.wireOp",EDGE,"E16"),sQuery(id+"F0.wireOp",EDGE,"E17"),sQuery(id+"F0.wireOp",EDGE,"E20"),sQuery(id+"F0.wireOp",EDGE,"E21"),sQuery(id+"F0.wireOp",EDGE,"E22"),sQuery(id+"F0.wireOp",EDGE,"E23"),sQuery(id+"F0.wireOp",EDGE,"E26"),sQuery(id+"F0.wireOp",EDGE,"E27"),sQuery(id+"F0.wireOp",EDGE,"E28"),sQuery(id+"F0.wireOp",EDGE,"E29"),sQuery(id+"F0.wireOp",EDGE,"E32"),sQuery(id+"F0.wireOp",EDGE,"E33"),sQuery(id+"F0.wireOp",EDGE,"E34"),sQuery(id+"F0.wireOp",EDGE,"E35"),sQuery(id+"F0.wireOp",EDGE,"E38"),sQuery(id+"F0.wireOp",EDGE,"E39"),sQuery(id+"F0.wireOp",EDGE,"E40"),sQuery(id+"F0.wireOp",EDGE,"E41"),sQuery(id+"F0.wireOp",EDGE,"E49"),sQuery(id+"F0.wireOp",EDGE,"E51"),subQ0,subQ1,sQuery(id+"F0.wireOp",EDGE,"E56.trimOffspring"),sQuery(id+"F0.wireOp",EDGE,"E57"),sQuery(id+"F0.wireOp",EDGE,"E58"),sQuery(id+"F0.wireOp",EDGE,"E59"),sQuery(id+"F0.wireOp",EDGE,"E60")])],"isStart":false})]});}
            var Q2;
            Q2=makeQuery(id+"F1.opExtrude","CAP_EDGE",EDGE,{"disambiguationData":[OSD([sQuery(id+"F0.wireOp",EDGE,"E58")])],"isStart":false});
            var Q3;
            Q3=makeQuery(id+"F1.opExtrude","CAP_EDGE",EDGE,{"disambiguationData":[OSD([sQuery(id+"F0.wireOp",EDGE,"E60")])],"isStart":false});
            var Q4;
            {var subQ0=sQuery(id+"F0.wireOp",EDGE,"E55");var subQ1=sQuery(id+"F0.wireOp",EDGE,"E56.trimOffspring");Q4=makeQuery(id+"F3.opFillet","BLEND_EDGE",EDGE,{"blendedFrom":[makeQuery(id+"F2.opExtrude","SWEPT_EDGE",EDGE,{"disambiguationData":[OSD([subQ0,subQ1])]}),makeQuery(id+"F1.opExtrude","CAP_FACE",FACE,{"disambiguationData":[OSD([sQuery(id+"F0.wireOp",EDGE,"E0"),sQuery(id+"F0.wireOp",EDGE,"E1"),sQuery(id+"F0.wireOp",EDGE,"E8"),sQuery(id+"F0.wireOp",EDGE,"E9"),sQuery(id+"F0.wireOp",EDGE,"E10"),sQuery(id+"F0.wireOp",EDGE,"E11"),sQuery(id+"F0.wireOp",EDGE,"E14"),sQuery(id+"F0.wireOp",EDGE,"E15"),sQuery(id+"F0.wireOp",EDGE,"E16"),sQuery(id+"F0.wireOp",EDGE,"E17"),sQuery(id+"F0.wireOp",EDGE,"E20"),sQuery(id+"F0.wireOp",EDGE,"E21"),sQuery(id+"F0.wireOp",EDGE,"E22"),sQuery(id+"F0.wireOp",EDGE,"E23"),sQuery(id+"F0.wireOp",EDGE,"E26"),sQuery(id+"F0.wireOp",EDGE,"E27"),sQuery(id+"F0.wireOp",EDGE,"E28"),sQuery(id+"F0.wireOp",EDGE,"E29"),sQuery(id+"F0.wireOp",EDGE,"E32"),sQuery(id+"F0.wireOp",EDGE,"E33"),sQuery(id+"F0.wireOp",EDGE,"E34"),sQuery(id+"F0.wireOp",EDGE,"E35"),sQuery(id+"F0.wireOp",EDGE,"E38"),sQuery(id+"F0.wireOp",EDGE,"E39"),sQuery(id+"F0.wireOp",EDGE,"E40"),sQuery(id+"F0.wireOp",EDGE,"E41"),sQuery(id+"F0.wireOp",EDGE,"E49"),sQuery(id+"F0.wireOp",EDGE,"E51"),sQuery(id+"F0.wireOp",EDGE,"E54"),subQ0,subQ1,sQuery(id+"F0.wireOp",EDGE,"E57"),sQuery(id+"F0.wireOp",EDGE,"E58"),sQuery(id+"F0.wireOp",EDGE,"E59"),sQuery(id+"F0.wireOp",EDGE,"E60")])],"isStart":false})],"blendedInto":[makeQuery(id+"F1.opExtrude","CAP_FACE",FACE,{"disambiguationData":[OSD([sQuery(id+"F0.wireOp",EDGE,"E0"),sQuery(id+"F0.wireOp",EDGE,"E1"),sQuery(id+"F0.wireOp",EDGE,"E8"),sQuery(id+"F0.wireOp",EDGE,"E9"),sQuery(id+"F0.wireOp",EDGE,"E10"),sQuery(id+"F0.wireOp",EDGE,"E11"),sQuery(id+"F0.wireOp",EDGE,"E14"),sQuery(id+"F0.wireOp",EDGE,"E15"),sQuery(id+"F0.wireOp",EDGE,"E16"),sQuery(id+"F0.wireOp",EDGE,"E17"),sQuery(id+"F0.wireOp",EDGE,"E20"),sQuery(id+"F0.wireOp",EDGE,"E21"),sQuery(id+"F0.wireOp",EDGE,"E22"),sQuery(id+"F0.wireOp",EDGE,"E23"),sQuery(id+"F0.wireOp",EDGE,"E26"),sQuery(id+"F0.wireOp",EDGE,"E27"),sQuery(id+"F0.wireOp",EDGE,"E28"),sQuery(id+"F0.wireOp",EDGE,"E29"),sQuery(id+"F0.wireOp",EDGE,"E32"),sQuery(id+"F0.wireOp",EDGE,"E33"),sQuery(id+"F0.wireOp",EDGE,"E34"),sQuery(id+"F0.wireOp",EDGE,"E35"),sQuery(id+"F0.wireOp",EDGE,"E38"),sQuery(id+"F0.wireOp",EDGE,"E39"),sQuery(id+"F0.wireOp",EDGE,"E40"),sQuery(id+"F0.wireOp",EDGE,"E41"),sQuery(id+"F0.wireOp",EDGE,"E49"),sQuery(id+"F0.wireOp",EDGE,"E51"),sQuery(id+"F0.wireOp",EDGE,"E54"),subQ0,subQ1,sQuery(id+"F0.wireOp",EDGE,"E57"),sQuery(id+"F0.wireOp",EDGE,"E58"),sQuery(id+"F0.wireOp",EDGE,"E59"),sQuery(id+"F0.wireOp",EDGE,"E60")])],"isStart":false})]});}
            var Q5;
            {var subQ0=sQuery(id+"F0.wireOp",EDGE,"E59");var subQ1=sQuery(id+"F0.wireOp",EDGE,"E60");Q5=makeQuery(id+"F10.opFillet","BLEND_EDGE",EDGE,{"blendedFrom":[makeQuery(id+"F2.opExtrude","SWEPT_EDGE",EDGE,{"disambiguationData":[OSD([subQ0,subQ1])]}),makeQuery(id+"F1.opExtrude","CAP_FACE",FACE,{"disambiguationData":[OSD([sQuery(id+"F0.wireOp",EDGE,"E0"),sQuery(id+"F0.wireOp",EDGE,"E1"),sQuery(id+"F0.wireOp",EDGE,"E8"),sQuery(id+"F0.wireOp",EDGE,"E9"),sQuery(id+"F0.wireOp",EDGE,"E10"),sQuery(id+"F0.wireOp",EDGE,"E11"),sQuery(id+"F0.wireOp",EDGE,"E14"),sQuery(id+"F0.wireOp",EDGE,"E15"),sQuery(id+"F0.wireOp",EDGE,"E16"),sQuery(id+"F0.wireOp",EDGE,"E17"),sQuery(id+"F0.wireOp",EDGE,"E20"),sQuery(id+"F0.wireOp",EDGE,"E21"),sQuery(id+"F0.wireOp",EDGE,"E22"),sQuery(id+"F0.wireOp",EDGE,"E23"),sQuery(id+"F0.wireOp",EDGE,"E26"),sQuery(id+"F0.wireOp",EDGE,"E27"),sQuery(id+"F0.wireOp",EDGE,"E28"),sQuery(id+"F0.wireOp",EDGE,"E29"),sQuery(id+"F0.wireOp",EDGE,"E32"),sQuery(id+"F0.wireOp",EDGE,"E33"),sQuery(id+"F0.wireOp",EDGE,"E34"),sQuery(id+"F0.wireOp",EDGE,"E35"),sQuery(id+"F0.wireOp",EDGE,"E38"),sQuery(id+"F0.wireOp",EDGE,"E39"),sQuery(id+"F0.wireOp",EDGE,"E40"),sQuery(id+"F0.wireOp",EDGE,"E41"),sQuery(id+"F0.wireOp",EDGE,"E49"),sQuery(id+"F0.wireOp",EDGE,"E51"),sQuery(id+"F0.wireOp",EDGE,"E54"),sQuery(id+"F0.wireOp",EDGE,"E55"),sQuery(id+"F0.wireOp",EDGE,"E56.trimOffspring"),sQuery(id+"F0.wireOp",EDGE,"E57"),sQuery(id+"F0.wireOp",EDGE,"E58"),subQ0,subQ1])],"isStart":false})],"blendedInto":[makeQuery(id+"F1.opExtrude","CAP_FACE",FACE,{"disambiguationData":[OSD([sQuery(id+"F0.wireOp",EDGE,"E0"),sQuery(id+"F0.wireOp",EDGE,"E1"),sQuery(id+"F0.wireOp",EDGE,"E8"),sQuery(id+"F0.wireOp",EDGE,"E9"),sQuery(id+"F0.wireOp",EDGE,"E10"),sQuery(id+"F0.wireOp",EDGE,"E11"),sQuery(id+"F0.wireOp",EDGE,"E14"),sQuery(id+"F0.wireOp",EDGE,"E15"),sQuery(id+"F0.wireOp",EDGE,"E16"),sQuery(id+"F0.wireOp",EDGE,"E17"),sQuery(id+"F0.wireOp",EDGE,"E20"),sQuery(id+"F0.wireOp",EDGE,"E21"),sQuery(id+"F0.wireOp",EDGE,"E22"),sQuery(id+"F0.wireOp",EDGE,"E23"),sQuery(id+"F0.wireOp",EDGE,"E26"),sQuery(id+"F0.wireOp",EDGE,"E27"),sQuery(id+"F0.wireOp",EDGE,"E28"),sQuery(id+"F0.wireOp",EDGE,"E29"),sQuery(id+"F0.wireOp",EDGE,"E32"),sQuery(id+"F0.wireOp",EDGE,"E33"),sQuery(id+"F0.wireOp",EDGE,"E34"),sQuery(id+"F0.wireOp",EDGE,"E35"),sQuery(id+"F0.wireOp",EDGE,"E38"),sQuery(id+"F0.wireOp",EDGE,"E39"),sQuery(id+"F0.wireOp",EDGE,"E40"),sQuery(id+"F0.wireOp",EDGE,"E41"),sQuery(id+"F0.wireOp",EDGE,"E49"),sQuery(id+"F0.wireOp",EDGE,"E51"),sQuery(id+"F0.wireOp",EDGE,"E54"),sQuery(id+"F0.wireOp",EDGE,"E55"),sQuery(id+"F0.wireOp",EDGE,"E56.trimOffspring"),sQuery(id+"F0.wireOp",EDGE,"E57"),sQuery(id+"F0.wireOp",EDGE,"E58"),subQ0,subQ1])],"isStart":false})]});}
            var Q6;
            {var subQ0=sQuery(id+"F0.wireOp",EDGE,"E57");var subQ1=sQuery(id+"F0.wireOp",EDGE,"E58");Q6=makeQuery(id+"F10.opFillet","BLEND_EDGE",EDGE,{"blendedFrom":[makeQuery(id+"F2.opExtrude","SWEPT_EDGE",EDGE,{"disambiguationData":[OSD([subQ0,subQ1])]}),makeQuery(id+"F1.opExtrude","CAP_FACE",FACE,{"disambiguationData":[OSD([sQuery(id+"F0.wireOp",EDGE,"E0"),sQuery(id+"F0.wireOp",EDGE,"E1"),sQuery(id+"F0.wireOp",EDGE,"E8"),sQuery(id+"F0.wireOp",EDGE,"E9"),sQuery(id+"F0.wireOp",EDGE,"E10"),sQuery(id+"F0.wireOp",EDGE,"E11"),sQuery(id+"F0.wireOp",EDGE,"E14"),sQuery(id+"F0.wireOp",EDGE,"E15"),sQuery(id+"F0.wireOp",EDGE,"E16"),sQuery(id+"F0.wireOp",EDGE,"E17"),sQuery(id+"F0.wireOp",EDGE,"E20"),sQuery(id+"F0.wireOp",EDGE,"E21"),sQuery(id+"F0.wireOp",EDGE,"E22"),sQuery(id+"F0.wireOp",EDGE,"E23"),sQuery(id+"F0.wireOp",EDGE,"E26"),sQuery(id+"F0.wireOp",EDGE,"E27"),sQuery(id+"F0.wireOp",EDGE,"E28"),sQuery(id+"F0.wireOp",EDGE,"E29"),sQuery(id+"F0.wireOp",EDGE,"E32"),sQuery(id+"F0.wireOp",EDGE,"E33"),sQuery(id+"F0.wireOp",EDGE,"E34"),sQuery(id+"F0.wireOp",EDGE,"E35"),sQuery(id+"F0.wireOp",EDGE,"E38"),sQuery(id+"F0.wireOp",EDGE,"E39"),sQuery(id+"F0.wireOp",EDGE,"E40"),sQuery(id+"F0.wireOp",EDGE,"E41"),sQuery(id+"F0.wireOp",EDGE,"E49"),sQuery(id+"F0.wireOp",EDGE,"E51"),sQuery(id+"F0.wireOp",EDGE,"E54"),sQuery(id+"F0.wireOp",EDGE,"E55"),sQuery(id+"F0.wireOp",EDGE,"E56.trimOffspring"),subQ0,subQ1,sQuery(id+"F0.wireOp",EDGE,"E59"),sQuery(id+"F0.wireOp",EDGE,"E60")])],"isStart":false})],"blendedInto":[makeQuery(id+"F1.opExtrude","CAP_FACE",FACE,{"disambiguationData":[OSD([sQuery(id+"F0.wireOp",EDGE,"E0"),sQuery(id+"F0.wireOp",EDGE,"E1"),sQuery(id+"F0.wireOp",EDGE,"E8"),sQuery(id+"F0.wireOp",EDGE,"E9"),sQuery(id+"F0.wireOp",EDGE,"E10"),sQuery(id+"F0.wireOp",EDGE,"E11"),sQuery(id+"F0.wireOp",EDGE,"E14"),sQuery(id+"F0.wireOp",EDGE,"E15"),sQuery(id+"F0.wireOp",EDGE,"E16"),sQuery(id+"F0.wireOp",EDGE,"E17"),sQuery(id+"F0.wireOp",EDGE,"E20"),sQuery(id+"F0.wireOp",EDGE,"E21"),sQuery(id+"F0.wireOp",EDGE,"E22"),sQuery(id+"F0.wireOp",EDGE,"E23"),sQuery(id+"F0.wireOp",EDGE,"E26"),sQuery(id+"F0.wireOp",EDGE,"E27"),sQuery(id+"F0.wireOp",EDGE,"E28"),sQuery(id+"F0.wireOp",EDGE,"E29"),sQuery(id+"F0.wireOp",EDGE,"E32"),sQuery(id+"F0.wireOp",EDGE,"E33"),sQuery(id+"F0.wireOp",EDGE,"E34"),sQuery(id+"F0.wireOp",EDGE,"E35"),sQuery(id+"F0.wireOp",EDGE,"E38"),sQuery(id+"F0.wireOp",EDGE,"E39"),sQuery(id+"F0.wireOp",EDGE,"E40"),sQuery(id+"F0.wireOp",EDGE,"E41"),sQuery(id+"F0.wireOp",EDGE,"E49"),sQuery(id+"F0.wireOp",EDGE,"E51"),sQuery(id+"F0.wireOp",EDGE,"E54"),sQuery(id+"F0.wireOp",EDGE,"E55"),sQuery(id+"F0.wireOp",EDGE,"E56.trimOffspring"),subQ0,subQ1,sQuery(id+"F0.wireOp",EDGE,"E59"),sQuery(id+"F0.wireOp",EDGE,"E60")])],"isStart":false})]});}
            fillet(context, id + "F14", {"entities" : qUnion([Q0, Q1, Q2, Q3, Q4, Q5, Q6]), "radius" : 5 * mm, "tangentPropagation" : true, "allowEdgeOverflow" : false});
        }
    });
